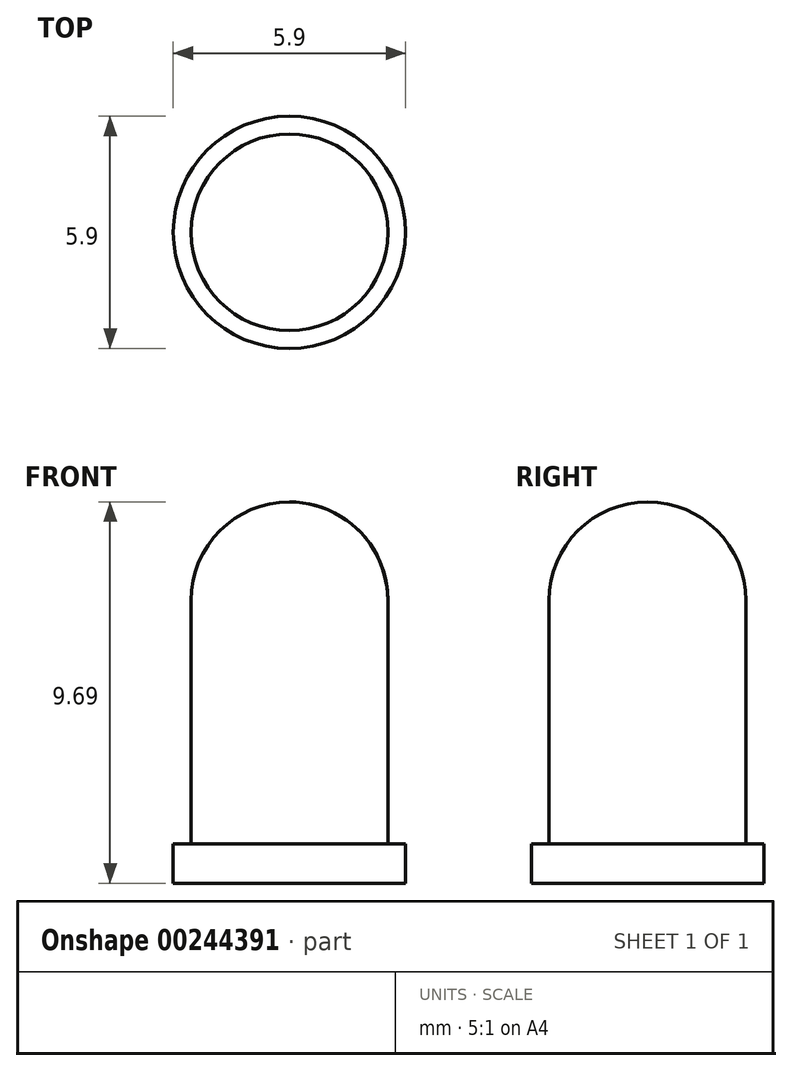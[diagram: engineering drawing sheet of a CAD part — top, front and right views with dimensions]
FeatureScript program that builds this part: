
annotation { "Feature Type Name" : "Feature", "Feature Type Description" : "" }
export const myFeature = defineFeature(function(context is Context, id is Id, definition is map)
    precondition{}
    {
        {
            var Q0;
            Q0=qCreatedBy(makeId("Front.planeOp"),FACE);
            var sketch = newSketch(context, id + "F0", { "sketchPlane" : qUnion([Q0])});
            skLineSegment(sketch, "E0", {"start": v(0, 0) * mm, "end": v(2.95, 0) * mm});
            skLineSegment(sketch, "E1", {"start": v(2.95, 0) * mm, "end": v(2.95, 1) * mm});
            skLineSegment(sketch, "E2", {"start": v(2.95, 1) * mm, "end": v(2.5, 1) * mm});
            skLineSegment(sketch, "E3", {"start": v(2.5, 1) * mm, "end": v(2.5, 7.2) * mm});
            skArc(sketch, "E4", {"start": v(2.5, 7.2) * mm, "mid": v(1.77, 8.96) * mm, "end": v(0, 9.7) * mm});
            skLineSegment(sketch, "E5", {"start": v(0, 0) * mm, "end": v(0, 9.7) * mm, "construction": true});
            skLineSegment(sketch, "E6", {"start": v(0, 9.7) * mm, "end": v(0, 0) * mm});
            skSolve(sketch);
        }
        {
            var Q0;
            Q0 = qSketchRegion(id + "F0", true);
            var Q1;
            Q1=sQuery(id+"F0.wireOp",EDGE,"E5");
            revolve(context, id + "F1", {"entities" : qUnion([Q0]), "axis" : qUnion([Q1]), "revolveType" : RevolveType.FULL});
        }
    });
